annotation { "Feature Type Name" : "Feature", "Feature Type Description" : "" }
export const myFeature = defineFeature(function(context is Context, id is Id, definition is map)
    precondition{}
    {
        {
            var Q0;
            Q0=qCreatedBy(makeId("Front.planeOp"),FACE);
            var sketch = newSketch(context, id + "F0", { "sketchPlane" : qUnion([Q0])});
            skLineSegment(sketch, "E0", {"start": v(0, 0) * mm, "end": v(0, 220) * mm});
            skLineSegment(sketch, "E1", {"start": v(0, 220) * mm, "end": v(-210, 220) * mm});
            skLineSegment(sketch, "E2", {"start": v(-210, 220) * mm, "end": v(-210, 439.77) * mm});
            skLineSegment(sketch, "E3", {"start": v(-210, 439.77) * mm, "end": v(-420, 439.77) * mm});
            skLineSegment(sketch, "E4", {"start": v(-420, 660) * mm, "end": v(-630, 660) * mm});
            skLineSegment(sketch, "E5", {"start": v(-630, 660) * mm, "end": v(-630, 880) * mm});
            skLineSegment(sketch, "E6", {"start": v(-630, 880) * mm, "end": v(-840, 880) * mm});
            skLineSegment(sketch, "E7", {"start": v(-840, 880) * mm, "end": v(-840, 1100.35) * mm});
            skLineSegment(sketch, "E8", {"start": v(-840, 1100.35) * mm, "end": v(-1130, 1100.35) * mm});
            skLineSegment(sketch, "E9", {"start": v(-1130, 1100.35) * mm, "end": v(-1130, 1020.35) * mm});
            skLineSegment(sketch, "E10", {"start": v(-1130, 1020.35) * mm, "end": v(-920, 1020.35) * mm});
            skLineSegment(sketch, "E11", {"start": v(-920, 1020.35) * mm, "end": v(-920, 800.35) * mm});
            skLineSegment(sketch, "E12", {"start": v(-920, 800.35) * mm, "end": v(-710, 800.35) * mm});
            skLineSegment(sketch, "E13", {"start": v(-710, 800.35) * mm, "end": v(-710, 580.35) * mm});
            skLineSegment(sketch, "E14", {"start": v(-710, 580.35) * mm, "end": v(-500, 580.35) * mm});
            skLineSegment(sketch, "E15", {"start": v(-420, 660) * mm, "end": v(-420, 439.77) * mm});
            skLineSegment(sketch, "E16", {"start": v(-500, 580.35) * mm, "end": v(-500, 360.35) * mm});
            skLineSegment(sketch, "E17", {"start": v(-500, 360.35) * mm, "end": v(-290, 360.35) * mm});
            skLineSegment(sketch, "E18", {"start": v(-290, 360.35) * mm, "end": v(-290, 140.35) * mm});
            skLineSegment(sketch, "E19", {"start": v(-290, 140.35) * mm, "end": v(-80, 140.35) * mm});
            skLineSegment(sketch, "E20.top", {"start": v(-80, 0) * mm, "end": v(0, 0) * mm});
            skLineSegment(sketch, "E20.left", {"start": v(-80, 140.35) * mm, "end": v(-80, 0) * mm});
            skLineSegment(sketch, "E21.bottom", {"start": v(-2578.83, 300.57) * mm, "end": v(-2075.03, 300.57) * mm});
            skLineSegment(sketch, "E21.top", {"start": v(-2578.83, 380.57) * mm, "end": v(-2075.03, 380.57) * mm});
            skLineSegment(sketch, "E21.left", {"start": v(-2578.83, 300.57) * mm, "end": v(-2578.83, 380.57) * mm});
            skLineSegment(sketch, "E21.right", {"start": v(-2075.03, 300.57) * mm, "end": v(-2075.03, 380.57) * mm});
            skLineSegment(sketch, "E22.bottom", {"start": v(-2075.03, 300.57) * mm, "end": v(-2155.03, 300.57) * mm});
            skLineSegment(sketch, "E22.top", {"start": v(-2075.03, 160.57) * mm, "end": v(-2155.03, 160.57) * mm});
            skLineSegment(sketch, "E22.left", {"start": v(-2075.03, 300.57) * mm, "end": v(-2075.03, 160.57) * mm});
            skLineSegment(sketch, "E22.right", {"start": v(-2155.03, 300.57) * mm, "end": v(-2155.03, 160.57) * mm});
            skLineSegment(sketch, "E23.bottom", {"start": v(-1348.37, -189.05) * mm, "end": v(-782.17, -189.05) * mm});
            skLineSegment(sketch, "E23.top", {"start": v(-1348.37, -109.05) * mm, "end": v(-782.17, -109.05) * mm});
            skLineSegment(sketch, "E23.left", {"start": v(-1348.37, -189.05) * mm, "end": v(-1348.37, -109.05) * mm});
            skLineSegment(sketch, "E23.right", {"start": v(-782.17, -189.05) * mm, "end": v(-782.17, -109.05) * mm});
            skLineSegment(sketch, "E24.bottom", {"start": v(-782.17, -189.05) * mm, "end": v(-862.17, -189.05) * mm});
            skLineSegment(sketch, "E24.top", {"start": v(-782.17, -189.05) * mm, "end": v(-862.17, -189.05) * mm});
            skLineSegment(sketch, "E24.left", {"start": v(-782.17, -189.05) * mm, "end": v(-782.17, -189.05) * mm});
            skLineSegment(sketch, "E24.right", {"start": v(-862.17, -189.05) * mm, "end": v(-862.17, -189.05) * mm});
            skLineSegment(sketch, "E25.bottom", {"start": v(-210, -394.28) * mm, "end": v(-130, -394.28) * mm});
            skLineSegment(sketch, "E25.top", {"start": v(-210, -174.28) * mm, "end": v(-130, -174.28) * mm});
            skLineSegment(sketch, "E25.left", {"start": v(-210, -394.28) * mm, "end": v(-210, -174.28) * mm});
            skLineSegment(sketch, "E25.right", {"start": v(-130, -394.28) * mm, "end": v(-130, -174.28) * mm});
            skLineSegment(sketch, "E26.bottom", {"start": v(-130, -394.28) * mm, "end": v(-210, -394.28) * mm});
            skLineSegment(sketch, "E27.bottom", {"start": v(362.53, -433.02) * mm, "end": v(968.73, -433.02) * mm});
            skLineSegment(sketch, "E27.top", {"start": v(362.53, -353.02) * mm, "end": v(968.73, -353.02) * mm});
            skLineSegment(sketch, "E27.left", {"start": v(362.53, -433.02) * mm, "end": v(362.53, -353.02) * mm});
            skLineSegment(sketch, "E27.right", {"start": v(968.73, -433.02) * mm, "end": v(968.73, -353.02) * mm});
            skLineSegment(sketch, "E28.bottom", {"start": v(968.73, -433.02) * mm, "end": v(888.73, -433.02) * mm});
            skLineSegment(sketch, "E28.top", {"start": v(968.73, -573.02) * mm, "end": v(888.73, -573.02) * mm});
            skLineSegment(sketch, "E28.left", {"start": v(968.73, -433.02) * mm, "end": v(968.73, -573.02) * mm});
            skLineSegment(sketch, "E28.right", {"start": v(888.73, -433.02) * mm, "end": v(888.73, -573.02) * mm});
            skLineSegment(sketch, "E29.bottom", {"start": v(948.78, -109.9) * mm, "end": v(1442.58, -109.9) * mm});
            skLineSegment(sketch, "E29.top", {"start": v(948.78, -29.9) * mm, "end": v(1442.58, -29.9) * mm});
            skLineSegment(sketch, "E29.left", {"start": v(948.78, -109.9) * mm, "end": v(948.78, -29.9) * mm});
            skLineSegment(sketch, "E29.right", {"start": v(1442.58, -109.9) * mm, "end": v(1442.58, -29.9) * mm});
            skLineSegment(sketch, "E30.bottom", {"start": v(1442.58, -109.9) * mm, "end": v(1362.58, -109.9) * mm});
            skLineSegment(sketch, "E30.top", {"start": v(1442.58, -249.9) * mm, "end": v(1362.58, -249.9) * mm});
            skLineSegment(sketch, "E30.left", {"start": v(1442.58, -109.9) * mm, "end": v(1442.58, -249.9) * mm});
            skLineSegment(sketch, "E30.right", {"start": v(1362.58, -109.9) * mm, "end": v(1362.58, -249.9) * mm});
            skLineSegment(sketch, "E31.bottom", {"start": v(1819.6, 126.54) * mm, "end": v(2199.8, 126.54) * mm});
            skLineSegment(sketch, "E31.top", {"start": v(1819.6, 206.54) * mm, "end": v(2199.8, 206.54) * mm});
            skLineSegment(sketch, "E31.left", {"start": v(1819.6, 126.54) * mm, "end": v(1819.6, 206.54) * mm});
            skLineSegment(sketch, "E31.right", {"start": v(2199.8, 126.54) * mm, "end": v(2199.8, 206.54) * mm});
            skLineSegment(sketch, "E32.bottom", {"start": v(2199.8, 126.54) * mm, "end": v(2119.8, 126.54) * mm});
            skLineSegment(sketch, "E32.top", {"start": v(2199.8, -13.46) * mm, "end": v(2119.8, -13.46) * mm});
            skLineSegment(sketch, "E32.left", {"start": v(2199.8, 126.54) * mm, "end": v(2199.8, -13.46) * mm});
            skLineSegment(sketch, "E32.right", {"start": v(2119.8, 126.54) * mm, "end": v(2119.8, -13.46) * mm});
            skLineSegment(sketch, "E33.bottom", {"start": v(2564.96, -275.66) * mm, "end": v(2724.96, -275.66) * mm});
            skLineSegment(sketch, "E33.top", {"start": v(2564.96, -195.66) * mm, "end": v(2724.96, -195.66) * mm});
            skLineSegment(sketch, "E33.left", {"start": v(2564.96, -275.66) * mm, "end": v(2564.96, -195.66) * mm});
            skLineSegment(sketch, "E33.right", {"start": v(2724.96, -275.66) * mm, "end": v(2724.96, -195.66) * mm});
            skLineSegment(sketch, "E34.bottom", {"start": v(2724.96, -275.66) * mm, "end": v(2644.96, -275.66) * mm});
            skLineSegment(sketch, "E34.top", {"start": v(2724.96, -415.66) * mm, "end": v(2644.96, -415.66) * mm});
            skLineSegment(sketch, "E34.left", {"start": v(2724.96, -275.66) * mm, "end": v(2724.96, -415.66) * mm});
            skLineSegment(sketch, "E34.right", {"start": v(2644.96, -275.66) * mm, "end": v(2644.96, -415.66) * mm});
            skLineSegment(sketch, "E35.bottom", {"start": v(3270.46, -439.63) * mm, "end": v(3350.46, -439.63) * mm});
            skLineSegment(sketch, "E35.top", {"start": v(3270.46, -79.63) * mm, "end": v(3350.46, -79.63) * mm});
            skLineSegment(sketch, "E35.left", {"start": v(3270.46, -439.63) * mm, "end": v(3270.46, -79.63) * mm});
            skLineSegment(sketch, "E35.right", {"start": v(3350.46, -439.63) * mm, "end": v(3350.46, -79.63) * mm});
            skLineSegment(sketch, "E36.bottom", {"start": v(3922.36, -626.8) * mm, "end": v(4002.36, -626.8) * mm});
            skLineSegment(sketch, "E36.top", {"start": v(3922.36, -406.8) * mm, "end": v(4002.36, -406.8) * mm});
            skLineSegment(sketch, "E36.left", {"start": v(3922.36, -626.8) * mm, "end": v(3922.36, -406.8) * mm});
            skLineSegment(sketch, "E36.right", {"start": v(4002.36, -626.8) * mm, "end": v(4002.36, -406.8) * mm});
            skLineSegment(sketch, "E37.bottom", {"start": v(4584.73, -401.44) * mm, "end": v(4664.73, -401.44) * mm});
            skLineSegment(sketch, "E37.top", {"start": v(4584.73, -441.44) * mm, "end": v(4664.73, -441.44) * mm});
            skLineSegment(sketch, "E37.left", {"start": v(4584.73, -401.44) * mm, "end": v(4584.73, -441.44) * mm});
            skLineSegment(sketch, "E37.right", {"start": v(4664.73, -401.44) * mm, "end": v(4664.73, -441.44) * mm});
            skLineSegment(sketch, "E38.bottom", {"start": v(4664.73, -441.44) * mm, "end": v(4624.73, -441.44) * mm});
            skLineSegment(sketch, "E38.top", {"start": v(4664.73, -481.44) * mm, "end": v(4624.73, -481.44) * mm});
            skLineSegment(sketch, "E38.left", {"start": v(4664.73, -441.44) * mm, "end": v(4664.73, -481.44) * mm});
            skLineSegment(sketch, "E38.right", {"start": v(4624.73, -441.44) * mm, "end": v(4624.73, -481.44) * mm});
            skLineSegment(sketch, "E39.bottom", {"start": v(5084.64, -413.66) * mm, "end": v(5234.64, -413.66) * mm});
            skLineSegment(sketch, "E39.top", {"start": v(5084.64, -493.66) * mm, "end": v(5234.64, -493.66) * mm});
            skLineSegment(sketch, "E39.left", {"start": v(5084.64, -413.66) * mm, "end": v(5084.64, -493.66) * mm});
            skLineSegment(sketch, "E39.right", {"start": v(5234.64, -413.66) * mm, "end": v(5234.64, -493.66) * mm});
            skLineSegment(sketch, "E40.bottom", {"start": v(5234.64, -493.66) * mm, "end": v(5154.64, -493.66) * mm});
            skLineSegment(sketch, "E40.top", {"start": v(5234.64, -633.66) * mm, "end": v(5154.64, -633.66) * mm});
            skLineSegment(sketch, "E40.left", {"start": v(5234.64, -493.66) * mm, "end": v(5234.64, -633.66) * mm});
            skLineSegment(sketch, "E40.right", {"start": v(5154.64, -493.66) * mm, "end": v(5154.64, -633.66) * mm});
            skLineSegment(sketch, "E41.bottom", {"start": v(-1357.39, 3328.86) * mm, "end": v(-822.39, 3328.86) * mm});
            skLineSegment(sketch, "E41.top", {"start": v(-1357.39, 3408.86) * mm, "end": v(-822.39, 3408.86) * mm});
            skLineSegment(sketch, "E41.left", {"start": v(-1357.39, 3328.86) * mm, "end": v(-1357.39, 3408.86) * mm});
            skLineSegment(sketch, "E41.right", {"start": v(-822.39, 3328.86) * mm, "end": v(-822.39, 3408.86) * mm});
            skLineSegment(sketch, "E42.bottom", {"start": v(-822.39, 3328.86) * mm, "end": v(-902.39, 3328.86) * mm});
            skLineSegment(sketch, "E42.top", {"start": v(-822.39, 3188.86) * mm, "end": v(-902.39, 3188.86) * mm});
            skLineSegment(sketch, "E42.left", {"start": v(-822.39, 3328.86) * mm, "end": v(-822.39, 3188.86) * mm});
            skLineSegment(sketch, "E42.right", {"start": v(-902.39, 3328.86) * mm, "end": v(-902.39, 3188.86) * mm});
            skLineSegment(sketch, "E43.bottom", {"start": v(-362.9, 3377.98) * mm, "end": v(132.1, 3377.98) * mm});
            skLineSegment(sketch, "E43.top", {"start": v(-362.9, 3457.98) * mm, "end": v(132.1, 3457.98) * mm});
            skLineSegment(sketch, "E43.left", {"start": v(-362.9, 3377.98) * mm, "end": v(-362.9, 3457.98) * mm});
            skLineSegment(sketch, "E43.right", {"start": v(132.1, 3377.98) * mm, "end": v(132.1, 3457.98) * mm});
            skLineSegment(sketch, "E44.bottom", {"start": v(132.1, 3377.98) * mm, "end": v(52.1, 3377.98) * mm});
            skLineSegment(sketch, "E44.top", {"start": v(132.1, 3237.98) * mm, "end": v(52.1, 3237.98) * mm});
            skLineSegment(sketch, "E44.left", {"start": v(132.1, 3377.98) * mm, "end": v(132.1, 3237.98) * mm});
            skLineSegment(sketch, "E44.right", {"start": v(52.1, 3377.98) * mm, "end": v(52.1, 3237.98) * mm});
            skLineSegment(sketch, "E45.bottom", {"start": v(416.79, 3352.05) * mm, "end": v(931.79, 3352.05) * mm});
            skLineSegment(sketch, "E45.top", {"start": v(416.79, 3432.05) * mm, "end": v(931.79, 3432.05) * mm});
            skLineSegment(sketch, "E45.left", {"start": v(416.79, 3352.05) * mm, "end": v(416.79, 3432.05) * mm});
            skLineSegment(sketch, "E45.right", {"start": v(931.79, 3352.05) * mm, "end": v(931.79, 3432.05) * mm});
            skLineSegment(sketch, "E46.bottom", {"start": v(931.79, 3352.05) * mm, "end": v(851.79, 3352.05) * mm});
            skLineSegment(sketch, "E46.top", {"start": v(931.79, 3132.05) * mm, "end": v(851.79, 3132.05) * mm});
            skLineSegment(sketch, "E46.left", {"start": v(931.79, 3352.05) * mm, "end": v(931.79, 3132.05) * mm});
            skLineSegment(sketch, "E46.right", {"start": v(851.79, 3352.05) * mm, "end": v(851.79, 3132.05) * mm});
            skLineSegment(sketch, "E47.bottom", {"start": v(1406.19, 3471.6) * mm, "end": v(1841.19, 3471.6) * mm});
            skLineSegment(sketch, "E47.top", {"start": v(1406.19, 3551.6) * mm, "end": v(1841.19, 3551.6) * mm});
            skLineSegment(sketch, "E47.left", {"start": v(1406.19, 3471.6) * mm, "end": v(1406.19, 3551.6) * mm});
            skLineSegment(sketch, "E47.right", {"start": v(1841.19, 3471.6) * mm, "end": v(1841.19, 3551.6) * mm});
            skLineSegment(sketch, "E48.bottom", {"start": v(1841.19, 3471.6) * mm, "end": v(1761.19, 3471.6) * mm});
            skLineSegment(sketch, "E48.top", {"start": v(1841.19, 3331.6) * mm, "end": v(1761.19, 3331.6) * mm});
            skLineSegment(sketch, "E48.left", {"start": v(1841.19, 3471.6) * mm, "end": v(1841.19, 3331.6) * mm});
            skLineSegment(sketch, "E48.right", {"start": v(1761.19, 3471.6) * mm, "end": v(1761.19, 3331.6) * mm});
            skLineSegment(sketch, "E49.bottom", {"start": v(2616.38, 4182.89) * mm, "end": v(2536.38, 4182.89) * mm});
            skLineSegment(sketch, "E49.top", {"start": v(2616.38, 3302.89) * mm, "end": v(2536.38, 3302.89) * mm});
            skLineSegment(sketch, "E49.left", {"start": v(2616.38, 4182.89) * mm, "end": v(2616.38, 3302.89) * mm});
            skLineSegment(sketch, "E49.right", {"start": v(2536.38, 4182.89) * mm, "end": v(2536.38, 3302.89) * mm});
            skSolve(sketch);
        }
        {
            var Q0;
            Q0=qSketchRegion(id+"F0",true);
            extrude(context, id + "F1", {"entities" : qUnion([Q0]), "depth" : 40 * mm, "offsetDistance" : 25 * mm});
        }
        {
            var Q0;
            Q0=qCreatedBy(makeId("Front.planeOp"),FACE);
            var sketch = newSketch(context, id + "F2", { "sketchPlane" : qUnion([Q0])});
            skLineSegment(sketch, "E50.bottom", {"start": v(-682.97, -92.7) * mm, "end": v(-432.97, -92.7) * mm});
            skLineSegment(sketch, "E50.top", {"start": v(-682.97, -132.7) * mm, "end": v(-432.97, -132.7) * mm});
            skLineSegment(sketch, "E50.left", {"start": v(-682.97, -92.7) * mm, "end": v(-682.97, -132.7) * mm});
            skLineSegment(sketch, "E50.right", {"start": v(-432.97, -92.7) * mm, "end": v(-432.97, -132.7) * mm});
            skSolve(sketch);
        }
        {
            var Q0;
            Q0=makeQuery(id+"F2.imprint","IMPRINT",FACE,{"disambiguationData":[TD([[makeQuery(id+"F2.imprint","IMPRINT",EDGE,{"derivedFrom":sQuery(id+"F2.wireOp",EDGE,"E50.bottom")}),-1.0]])]});
            extrude(context, id + "F3", {"entities" : qUnion([Q0]), "depth" : 830 * mm, "offsetDistance" : 25 * mm});
        }
        {
            var Q0;
            Q0=qCreatedBy(makeId("Top.planeOp"),FACE);
            var sketch = newSketch(context, id + "F4", { "sketchPlane" : qUnion([Q0])});
            skLineSegment(sketch, "E51.top", {"start": v(-47.98, 505.23) * mm, "end": v(812.02, 505.23) * mm});
            skLineSegment(sketch, "E51.right", {"start": v(812.02, -544.77) * mm, "end": v(812.02, 505.23) * mm});
            skLineSegment(sketch, "E52", {"start": v(-47.98, -374.77) * mm, "end": v(-47.98, 505.23) * mm});
            skLineSegment(sketch, "E53", {"start": v(32.02, -544.77) * mm, "end": v(812.02, -544.77) * mm});
            skLineSegment(sketch, "E54", {"start": v(32.02, -518.77) * mm, "end": v(812.02, -265.33) * mm});
            skLineSegment(sketch, "E55", {"start": v(32.02, -486.64) * mm, "end": v(812.02, 80.06) * mm});
            skLineSegment(sketch, "E56", {"start": v(32.02, -434.66) * mm, "end": v(714.89, 505.23) * mm});
            skLineSegment(sketch, "E57", {"start": v(7.26, -374.77) * mm, "end": v(293.18, 505.23) * mm});
            skLineSegment(sketch, "E58.top", {"start": v(-47.98, -374.77) * mm, "end": v(32.02, -374.77) * mm});
            skLineSegment(sketch, "E58.right", {"start": v(32.02, -544.77) * mm, "end": v(32.02, -374.77) * mm});
            skLineSegment(sketch, "E59.top", {"start": v(-2332.02, 1857.89) * mm, "end": v(-1472.02, 1857.89) * mm});
            skLineSegment(sketch, "E59.right", {"start": v(-1472.02, 807.89) * mm, "end": v(-1472.02, 1857.89) * mm});
            skLineSegment(sketch, "E60", {"start": v(-2332.02, 807.89) * mm, "end": v(-2332.02, 1857.89) * mm});
            skLineSegment(sketch, "E61", {"start": v(-2332.02, 807.89) * mm, "end": v(-1472.02, 807.89) * mm});
            skLineSegment(sketch, "E62", {"start": v(-2332.02, 807.89) * mm, "end": v(-618.07, 1364.79) * mm});
            skLineSegment(sketch, "E63", {"start": v(-2332.02, 807.89) * mm, "end": v(-904.42, 1845.1) * mm});
            skLineSegment(sketch, "E64", {"start": v(-2332.02, 807.89) * mm, "end": v(-1124.73, 2469.58) * mm});
            skLineSegment(sketch, "E65", {"start": v(-2332.02, 807.89) * mm, "end": v(-1660.21, 2875.5) * mm});
            skLineSegment(sketch, "E66.bottom", {"start": v(-2332.02, 807.89) * mm, "end": v(-1818.46, 807.89) * mm});
            skLineSegment(sketch, "E66.top", {"start": v(-2332.02, 1051.9) * mm, "end": v(-1818.46, 1051.9) * mm});
            skLineSegment(sketch, "E66.left", {"start": v(-2332.02, 807.89) * mm, "end": v(-2332.02, 1051.9) * mm});
            skLineSegment(sketch, "E66.right", {"start": v(-1818.46, 807.89) * mm, "end": v(-1818.46, 1051.9) * mm});
            skLineSegment(sketch, "E67.top", {"start": v(1615.02, -757.08) * mm, "end": v(2475.02, -757.08) * mm});
            skLineSegment(sketch, "E67.right", {"start": v(2475.02, -1807.08) * mm, "end": v(2475.02, -757.08) * mm});
            skLineSegment(sketch, "E68", {"start": v(1615.02, -1807.08) * mm, "end": v(1615.02, -757.08) * mm});
            skLineSegment(sketch, "E69", {"start": v(1615.02, -1807.08) * mm, "end": v(2475.02, -1807.08) * mm});
            skLineSegment(sketch, "E70", {"start": v(1615.02, -1807.08) * mm, "end": v(3328.97, -1250.18) * mm});
            skLineSegment(sketch, "E71", {"start": v(1615.02, -1807.08) * mm, "end": v(3042.62, -769.87) * mm});
            skLineSegment(sketch, "E72", {"start": v(1615.02, -1807.08) * mm, "end": v(2822.3, -145.4) * mm});
            skLineSegment(sketch, "E73", {"start": v(1615.02, -1807.08) * mm, "end": v(2286.82, 260.52) * mm});
            skLineSegment(sketch, "E74.bottom", {"start": v(1615.02, -1807.08) * mm, "end": v(1695.02, -1807.08) * mm});
            skLineSegment(sketch, "E74.top", {"start": v(1615.02, -1637.08) * mm, "end": v(1695.02, -1637.08) * mm});
            skLineSegment(sketch, "E74.left", {"start": v(1615.02, -1807.08) * mm, "end": v(1615.02, -1637.08) * mm});
            skLineSegment(sketch, "E74.right", {"start": v(1695.02, -1807.08) * mm, "end": v(1695.02, -1637.08) * mm});
            skLineSegment(sketch, "E75.right", {"start": v(472.23, -2101.59) * mm, "end": v(472.23, -1822.16) * mm});
            skLineSegment(sketch, "E76", {"start": v(-307.77, -2101.59) * mm, "end": v(472.23, -2101.59) * mm});
            skLineSegment(sketch, "E77", {"start": v(-307.77, -2075.6) * mm, "end": v(472.23, -1822.16) * mm});
            skLineSegment(sketch, "E78", {"start": v(-307.77, -2043.46) * mm, "end": v(472.23, -1476.76) * mm});
            skLineSegment(sketch, "E79", {"start": v(-332.53, -1931.59) * mm, "end": v(-46.6, -1051.59) * mm});
            skLineSegment(sketch, "E80.right", {"start": v(-307.77, -2101.59) * mm, "end": v(-307.77, -2075.6) * mm});
            skLineSegment(sketch, "E81.trimOffspring", {"start": v(472.23, -1476.76) * mm, "end": v(472.23, -1051.59) * mm});
            skLineSegment(sketch, "E82", {"start": v(-653.82, -4085.18) * mm, "end": v(29.05, -3145.3) * mm});
            skLineSegment(sketch, "E83.trimOffspring", {"start": v(-653.82, -4085.18) * mm, "end": v(-653.82, -4025.3) * mm});
            skLineSegment(sketch, "E84.0", {"start": v(-462.27, -1931.59) * mm, "end": v(-462.27, -1051.59) * mm});
            skLineSegment(sketch, "E85", {"start": v(-462.27, -1931.59) * mm, "end": v(-332.53, -1931.59) * mm});
            skLineSegment(sketch, "E86", {"start": v(-462.27, -1051.59) * mm, "end": v(-46.6, -1051.59) * mm});
            skText(sketch, "E87", { "text": "GOTOWE\n", "fontName": "OpenSans-Regular.ttf"});
            skLineSegment(sketch, "E88", {"start": v(-653.82, -4025.3) * mm, "end": v(-720.64, -4025.3) * mm});
            skLineSegment(sketch, "E89", {"start": v(-434.71, -3145.3) * mm, "end": v(29.05, -3145.3) * mm});
            skLineSegment(sketch, "E90", {"start": v(-720.64, -4025.3) * mm, "end": v(-434.71, -3145.3) * mm});
            skLineSegment(sketch, "E91.0", {"start": v(-307.77, -1923.42) * mm, "end": v(325.66, -1051.59) * mm});
            skLineSegment(sketch, "E92", {"start": v(325.66, -1051.59) * mm, "end": v(472.23, -1051.59) * mm});
            skLineSegment(sketch, "E93", {"start": v(-307.77, -1923.42) * mm, "end": v(-307.77, -2043.46) * mm});
            skLineSegment(sketch, "E94.right", {"start": v(1369.34, -4712.42) * mm, "end": v(1369.34, -4367.03) * mm});
            skLineSegment(sketch, "E95", {"start": v(589.34, -4965.86) * mm, "end": v(1369.34, -4712.42) * mm});
            skLineSegment(sketch, "E96.right", {"start": v(589.34, -4965.86) * mm, "end": v(589.34, -4933.73) * mm});
            skLineSegment(sketch, "E97", {"start": v(589.34, -4933.73) * mm, "end": v(589.34, -4884.29) * mm});
            skLineSegment(sketch, "E98", {"start": v(1369.34, -4367.03) * mm, "end": v(1369.34, -4317.58) * mm});
            skLineSegment(sketch, "E99", {"start": v(589.34, -4884.29) * mm, "end": v(1369.34, -4317.58) * mm});
            skLineSegment(sketch, "E100.right", {"start": v(-1409.89, -2528.05) * mm, "end": v(-1409.89, -2248.62) * mm});
            skLineSegment(sketch, "E101", {"start": v(-2189.89, -2528.05) * mm, "end": v(-1409.89, -2528.05) * mm});
            skLineSegment(sketch, "E102.right", {"start": v(-2189.89, -2528.05) * mm, "end": v(-2189.89, -2502.06) * mm});
            skLineSegment(sketch, "E103.0", {"start": v(-2189.89, -2460) * mm, "end": v(-1422.25, -2210.58) * mm});
            skLineSegment(sketch, "E104", {"start": v(-2189.89, -2528.05) * mm, "end": v(-2189.89, -2460) * mm});
            skLineSegment(sketch, "E105", {"start": v(-1409.89, -2528.05) * mm, "end": v(-1409.89, -2206.56) * mm});
            skLineSegment(sketch, "E106", {"start": v(-1422.25, -2210.58) * mm, "end": v(-1409.89, -2206.56) * mm});
            skLineSegment(sketch, "E107.top", {"start": v(4345.64, 540.9) * mm, "end": v(4775.64, 540.9) * mm});
            skLineSegment(sketch, "E107.left", {"start": v(4345.64, 80.9) * mm, "end": v(4345.64, 540.9) * mm});
            skLineSegment(sketch, "E107.right", {"start": v(5205.64, -379.1) * mm, "end": v(5205.64, 540.9) * mm});
            skLineSegment(sketch, "E108", {"start": v(5205.64, -379.1) * mm, "end": v(4345.64, -379.1) * mm});
            skLineSegment(sketch, "E109", {"start": v(5205.64, -379.1) * mm, "end": v(4345.64, 540.9) * mm});
            skLineSegment(sketch, "E110", {"start": v(5205.64, -379.1) * mm, "end": v(4345.64, 80.9) * mm});
            skLineSegment(sketch, "E111", {"start": v(5205.64, -379.1) * mm, "end": v(4775.64, 540.9) * mm});
            skLineSegment(sketch, "E112", {"start": v(4775.64, 540.9) * mm, "end": v(5205.64, 540.9) * mm});
            skPoint(sketch, "E113.orphan", {"position": v(4345.64, -379.1) * mm});
            skLineSegment(sketch, "E114", {"start": v(4345.64, 80.9) * mm, "end": v(4345.64, -379.1) * mm});
            skLineSegment(sketch, "E115.bottom", {"start": v(5205.64, -379.1) * mm, "end": v(5125.64, -379.1) * mm});
            skLineSegment(sketch, "E115.top", {"start": v(5205.64, -339.1) * mm, "end": v(5125.64, -339.1) * mm});
            skLineSegment(sketch, "E115.left", {"start": v(5205.64, -379.1) * mm, "end": v(5205.64, -339.1) * mm});
            skLineSegment(sketch, "E115.right", {"start": v(5125.64, -379.1) * mm, "end": v(5125.64, -339.1) * mm});
            skLineSegment(sketch, "E116.right", {"start": v(9124.54, 1333.6) * mm, "end": v(9124.54, 2213.6) * mm});
            skLineSegment(sketch, "E117", {"start": v(8694.54, 2213.6) * mm, "end": v(9124.54, 2213.6) * mm});
            skLineSegment(sketch, "E118.top", {"start": v(9124.54, 1333.6) * mm, "end": v(9105.84, 1333.6) * mm});
            skLineSegment(sketch, "E119", {"start": v(10139.01, 171.77) * mm, "end": v(9316.4, 1051.77) * mm});
            skLineSegment(sketch, "E120.top", {"start": v(9713.88, 2351.53) * mm, "end": v(10143.88, 2351.53) * mm});
            skLineSegment(sketch, "E121", {"start": v(10555.18, 1471.53) * mm, "end": v(10143.88, 2351.53) * mm});
            skLineSegment(sketch, "E122.top", {"start": v(10555.18, 1471.53) * mm, "end": v(10536.49, 1471.53) * mm});
            skLineSegment(sketch, "E123", {"start": v(12382.63, 807.89) * mm, "end": v(11602.63, 807.89) * mm});
            skLineSegment(sketch, "E124", {"start": v(12387.85, 847.89) * mm, "end": v(11602.63, 1267.89) * mm});
            skPoint(sketch, "E125.orphan", {"position": v(11602.63, 807.89) * mm});
            skLineSegment(sketch, "E126", {"start": v(11602.63, 1267.89) * mm, "end": v(11602.63, 807.89) * mm});
            skLineSegment(sketch, "E127.right", {"start": v(12382.63, 807.89) * mm, "end": v(12382.63, 847.89) * mm});
            skLineSegment(sketch, "E128.trimOffspring", {"start": v(10139.01, 171.77) * mm, "end": v(10101.62, 171.77) * mm});
            skLineSegment(sketch, "E129.trimOffspring", {"start": v(12387.85, 847.89) * mm, "end": v(12382.63, 847.89) * mm});
            skLineSegment(sketch, "E130.0", {"start": v(9061.69, 1333.6) * mm, "end": v(8658.77, 2195.65) * mm});
            skLineSegment(sketch, "E131", {"start": v(8694.54, 2213.6) * mm, "end": v(8650.38, 2213.6) * mm});
            skLineSegment(sketch, "E132", {"start": v(9105.84, 1333.6) * mm, "end": v(9061.69, 1333.6) * mm});
            skLineSegment(sketch, "E133", {"start": v(8658.77, 2195.65) * mm, "end": v(8650.38, 2213.6) * mm});
            skLineSegment(sketch, "E134.0", {"start": v(10481.73, 1471.53) * mm, "end": v(9713.88, 2292.96) * mm});
            skLineSegment(sketch, "E135", {"start": v(10536.49, 1471.53) * mm, "end": v(10481.73, 1471.53) * mm});
            skLineSegment(sketch, "E136.0", {"start": v(10016.81, 171.77) * mm, "end": v(9316.4, 546.4) * mm});
            skLineSegment(sketch, "E137", {"start": v(10101.62, 171.77) * mm, "end": v(10016.81, 171.77) * mm});
            skLineSegment(sketch, "E138", {"start": v(9316.4, 1051.77) * mm, "end": v(9316.4, 546.4) * mm});
            skLineSegment(sketch, "E139", {"start": v(9713.88, 2351.53) * mm, "end": v(9713.88, 2292.96) * mm});
            skLineSegment(sketch, "E140", {"start": v(3639.4, -6062.46) * mm, "end": v(4419.4, -5495.76) * mm});
            skLineSegment(sketch, "E141.trimOffspring", {"start": v(4419.4, -5495.76) * mm, "end": v(4419.4, -5070.59) * mm});
            skLineSegment(sketch, "E142.0", {"start": v(3639.4, -5942.42) * mm, "end": v(4272.84, -5070.59) * mm});
            skLineSegment(sketch, "E143", {"start": v(4272.84, -5070.59) * mm, "end": v(4419.4, -5070.59) * mm});
            skLineSegment(sketch, "E144", {"start": v(3639.4, -5942.42) * mm, "end": v(3639.4, -6062.46) * mm});
            skLineSegment(sketch, "E145", {"start": v(7082.91, -6742.24) * mm, "end": v(7368.84, -5862.24) * mm});
            skLineSegment(sketch, "E146.0", {"start": v(6953.17, -6742.24) * mm, "end": v(6953.17, -5862.24) * mm});
            skLineSegment(sketch, "E147", {"start": v(6953.17, -6742.24) * mm, "end": v(7082.91, -6742.24) * mm});
            skLineSegment(sketch, "E148", {"start": v(6953.17, -5862.24) * mm, "end": v(7368.84, -5862.24) * mm});
            skLineSegment(sketch, "E149.bottom", {"start": v(3060.13, 3977.35) * mm, "end": v(3970.13, 3977.35) * mm});
            skLineSegment(sketch, "E149.top", {"start": v(3060.13, 4847.35) * mm, "end": v(3970.13, 4847.35) * mm});
            skLineSegment(sketch, "E149.left", {"start": v(3060.13, 3977.35) * mm, "end": v(3060.13, 4847.35) * mm});
            skLineSegment(sketch, "E149.right", {"start": v(3970.13, 3977.35) * mm, "end": v(3970.13, 4847.35) * mm});
            skLineSegment(sketch, "E150", {"start": v(3060.13, 4847.35) * mm, "end": v(3060.13, 5144) * mm});
            skLineSegment(sketch, "E151.0", {"start": v(3515.13, 4847.35) * mm, "end": v(3515.13, 5144) * mm});
            skLineSegment(sketch, "E152", {"start": v(3060.13, 4847.35) * mm, "end": v(2788.73, 4847.35) * mm});
            skLineSegment(sketch, "E153.0", {"start": v(3060.13, 4412.35) * mm, "end": v(2788.73, 4412.35) * mm});
            skLineSegment(sketch, "E154", {"start": v(3970.13, 3977.35) * mm, "end": v(3515.13, 4847.35) * mm});
            skLineSegment(sketch, "E155", {"start": v(3970.13, 3977.35) * mm, "end": v(3060.13, 4847.35) * mm});
            skLineSegment(sketch, "E156", {"start": v(3970.13, 3977.35) * mm, "end": v(3060.13, 4412.35) * mm});
            skLineSegment(sketch, "E157.top", {"start": v(5206.12, 5104.66) * mm, "end": v(5661.12, 5104.66) * mm});
            skLineSegment(sketch, "E157.right", {"start": v(5661.12, 4274.66) * mm, "end": v(5661.12, 5104.66) * mm});
            skLineSegment(sketch, "E158.top", {"start": v(5661.12, 4274.66) * mm, "end": v(5595.06, 4274.66) * mm});
            skLineSegment(sketch, "E159.bottom", {"start": v(3970.13, 3977.35) * mm, "end": v(3890.13, 3977.35) * mm});
            skLineSegment(sketch, "E159.top", {"start": v(3970.13, 4017.35) * mm, "end": v(3890.13, 4017.35) * mm});
            skLineSegment(sketch, "E159.left", {"start": v(3970.13, 3977.35) * mm, "end": v(3970.13, 4017.35) * mm});
            skLineSegment(sketch, "E159.right", {"start": v(3890.13, 3977.35) * mm, "end": v(3890.13, 4017.35) * mm});
            skLineSegment(sketch, "E160", {"start": v(5206.12, 5104.66) * mm, "end": v(5160.98, 5104.66) * mm});
            skLineSegment(sketch, "E161", {"start": v(5170.68, 5086.12) * mm, "end": v(5189.55, 5050.03) * mm});
            skLineSegment(sketch, "E162", {"start": v(5189.55, 5050.03) * mm, "end": v(5160.98, 5104.66) * mm});
            skLineSegment(sketch, "E163.trimOffspring", {"start": v(5595.06, 4274.66) * mm, "end": v(5170.68, 5086.12) * mm});
            skLineSegment(sketch, "E164.top", {"start": v(6822.3, 5560.33) * mm, "end": v(7277.3, 5560.33) * mm});
            skLineSegment(sketch, "E164.left", {"start": v(6822.3, 5505) * mm, "end": v(6822.3, 5560.33) * mm});
            skLineSegment(sketch, "E165", {"start": v(7711.38, 4730.33) * mm, "end": v(7277.3, 5560.33) * mm});
            skLineSegment(sketch, "E166.top", {"start": v(7711.38, 4730.33) * mm, "end": v(7652.3, 4730.33) * mm});
            skLineSegment(sketch, "E166.right", {"start": v(7652.3, 4711.48) * mm, "end": v(7652.3, 4730.33) * mm});
            skLineSegment(sketch, "E167.trimOffspring", {"start": v(7652.3, 4711.48) * mm, "end": v(6822.3, 5505) * mm});
            skLineSegment(sketch, "E168.left", {"start": v(8733.66, 5429.45) * mm, "end": v(8733.66, 5908.78) * mm});
            skLineSegment(sketch, "E169", {"start": v(9601.82, 5078.78) * mm, "end": v(8733.66, 5908.78) * mm});
            skLineSegment(sketch, "E170.right", {"start": v(9563.66, 5038.78) * mm, "end": v(9563.66, 5078.78) * mm});
            skLineSegment(sketch, "E171.trimOffspring", {"start": v(9601.82, 5078.78) * mm, "end": v(9563.66, 5078.78) * mm});
            skLineSegment(sketch, "E172.0", {"start": v(9546.41, 5040.93) * mm, "end": v(8733.66, 5429.45) * mm});
            skLineSegment(sketch, "E173", {"start": v(9563.66, 5038.78) * mm, "end": v(9550.91, 5038.78) * mm});
            skLineSegment(sketch, "E174", {"start": v(9546.41, 5040.93) * mm, "end": v(9550.91, 5038.78) * mm});
            skLineSegment(sketch, "E175.bottom", {"start": v(10726.24, 5385.35) * mm, "end": v(11556.24, 5385.35) * mm});
            skLineSegment(sketch, "E175.left", {"start": v(10726.24, 5385.35) * mm, "end": v(10726.24, 5820.35) * mm});
            skLineSegment(sketch, "E176", {"start": v(11556.24, 5423.6) * mm, "end": v(10726.24, 5820.35) * mm});
            skLineSegment(sketch, "E177.right", {"start": v(11556.24, 5385.35) * mm, "end": v(11556.24, 5423.6) * mm});
            const initialGuessF4  = {"E87": [4.11145, -3.47683, 1, 0, 0.4424]};
            skSetInitialGuess(sketch, initialGuessF4);
            skSolve(sketch);
        }
        {
            var Q0;
            Q0=makeQuery(id+"F4.imprint","IMPRINT",FACE,{"disambiguationData":[TD([[makeQuery(id+"F4.imprint","IMPRINT",EDGE,{"derivedFrom":sQuery(id+"F4.wireOp",EDGE,"E79")}),1.0]])]});
            extrude(context, id + "F5", {"entities" : qUnion([Q0]), "depth" : 40 * mm, "offsetDistance" : 25 * mm});
        }
        {
            var Q0;
            Q0=makeQuery(id+"F4.imprint","IMPRINT",FACE,{"disambiguationData":[TD([[makeQuery(id+"F4.imprint","IMPRINT",EDGE,{"derivedFrom":sQuery(id+"F4.wireOp",EDGE,"E82")}),1.0]])]});
            extrude(context, id + "F6", {"entities" : qUnion([Q0]), "depth" : 40 * mm, "offsetDistance" : 25 * mm});
        }
        {
            var Q0;
            Q0=makeQuery(id+"F4.imprint","IMPRINT",FACE,{"disambiguationData":[TD([[makeQuery(id+"F4.imprint","IMPRINT",EDGE,{"derivedFrom":sQuery(id+"F4.wireOp",EDGE,"E78")}),1.0]])]});
            extrude(context, id + "F7", {"entities" : qUnion([Q0]), "depth" : 40 * mm, "offsetDistance" : 25 * mm});
        }
        {
            var Q0;
            Q0=makeQuery(id+"F4.imprint","IMPRINT",FACE,{"disambiguationData":[TD([[makeQuery(id+"F4.imprint","IMPRINT",EDGE,{"derivedFrom":sQuery(id+"F4.wireOp",EDGE,"E94.right")}),1.0]])]});
            extrude(context, id + "F8", {"entities" : qUnion([Q0]), "depth" : 40 * mm, "offsetDistance" : 25 * mm});
        }
        {
            var Q0;
            {var subQ3=sQuery(id+"F4.wireOp",EDGE,"E101");Q0=makeQuery(id+"F4.imprint","IMPRINT",FACE,{"disambiguationData":[TD([[makeQuery(id+"F4.imprint","IMPRINT",EDGE,{"derivedFrom":subQ3}),1.0]])]});}
            extrude(context, id + "F9", {"entities" : qUnion([Q0]), "depth" : 40 * mm, "offsetDistance" : 25 * mm});
        }
        {
            var Q0;
            Q0=makeQuery(id+"F4.imprint","IMPRINT",FACE,{"disambiguationData":[TD([[makeQuery(id+"F4.imprint","IMPRINT",EDGE,{"derivedFrom":sQuery(id+"F4.wireOp",EDGE,"E116.right")}),1.0]])]});
            extrude(context, id + "F10", {"entities" : qUnion([Q0]), "depth" : 40 * mm, "offsetDistance" : 25 * mm});
        }
        {
            var Q0;
            Q0=makeQuery(id+"F4.imprint","IMPRINT",FACE,{"disambiguationData":[TD([[makeQuery(id+"F4.imprint","IMPRINT",EDGE,{"derivedFrom":sQuery(id+"F4.wireOp",EDGE,"E120.top")}),-1.0]])]});
            extrude(context, id + "F11", {"entities" : qUnion([Q0]), "depth" : 25 * mm, "offsetDistance" : 25 * mm});
        }
        {
            var Q0;
            Q0=makeQuery(id+"F4.imprint","IMPRINT",FACE,{"disambiguationData":[TD([[makeQuery(id+"F4.imprint","IMPRINT",EDGE,{"derivedFrom":sQuery(id+"F4.wireOp",EDGE,"E119")}),1.0]])]});
            extrude(context, id + "F12", {"entities" : qUnion([Q0]), "depth" : 40 * mm, "offsetDistance" : 25 * mm});
        }
        {
            var Q0;
            Q0=makeQuery(id+"F4.imprint","IMPRINT",FACE,{"disambiguationData":[TD([[makeQuery(id+"F4.imprint","IMPRINT",EDGE,{"derivedFrom":sQuery(id+"F4.wireOp",EDGE,"E123")}),-1.0]])]});
            extrude(context, id + "F13", {"entities" : qUnion([Q0]), "depth" : 40 * mm, "offsetDistance" : 25 * mm});
        }
        {
            var Q0;
            Q0=makeQuery(id+"F0.imprint","IMPRINT",FACE,{"disambiguationData":[TD([[makeQuery(id+"F0.imprint","IMPRINT",EDGE,{"derivedFrom":sQuery(id+"F0.wireOp",EDGE,"E22.bottom")}),1.0]])]});
            var Q1;
            Q1=makeQuery(id+"F0.imprint","IMPRINT",FACE,{"disambiguationData":[TD([[makeQuery(id+"F0.imprint","IMPRINT",EDGE,{"derivedFrom":sQuery(id+"F0.wireOp",EDGE,"E21.bottom")}),1.0]])]});
            extrude(context, id + "F14", {"entities" : qUnion([Q0, Q1]), "operationType" : NewBodyOperationType.ADD, "depth" : 40 * mm, "offsetDistance" : 25 * mm});
        }
        {
            var Q0;
            Q0=makeQuery(id+"F0.imprint","IMPRINT",FACE,{"disambiguationData":[TD([[makeQuery(id+"F0.imprint","IMPRINT",EDGE,{"derivedFrom":sQuery(id+"F0.wireOp",EDGE,"E23.bottom")}),1.0]])]});
            var Q1;
            Q1=makeQuery(id+"F0.imprint","IMPRINT",FACE,{"disambiguationData":[TD([[makeQuery(id+"F0.imprint","IMPRINT",EDGE,{"derivedFrom":sQuery(id+"F0.wireOp",EDGE,"E24.bottom")}),1.0]])]});
            extrude(context, id + "F15", {"entities" : qUnion([Q0, Q1]), "operationType" : NewBodyOperationType.ADD, "depth" : 40 * mm, "offsetDistance" : 25 * mm});
        }
        {
            var Q0;
            Q0=makeQuery(id+"F0.imprint","IMPRINT",FACE,{"disambiguationData":[TD([[makeQuery(id+"F0.imprint","IMPRINT",EDGE,{"derivedFrom":sQuery(id+"F0.wireOp",EDGE,"E25.bottom")}),1.0]])]});
            var Q1;
            Q1=makeQuery(id+"F0.imprint","IMPRINT",FACE,{"disambiguationData":[TD([[makeQuery(id+"F0.imprint","IMPRINT",EDGE,{"derivedFrom":sQuery(id+"F0.wireOp",EDGE,"E26.bottom")}),1.0]])]});
            extrude(context, id + "F16", {"entities" : qUnion([Q0, Q1]), "operationType" : NewBodyOperationType.ADD, "depth" : 40 * mm, "offsetDistance" : 25 * mm});
        }
        {
            var Q0;
            Q0=makeQuery(id+"F0.imprint","IMPRINT",FACE,{"disambiguationData":[TD([[makeQuery(id+"F0.imprint","IMPRINT",EDGE,{"derivedFrom":sQuery(id+"F0.wireOp",EDGE,"E27.bottom")}),1.0]])]});
            var Q1;
            Q1=makeQuery(id+"F0.imprint","IMPRINT",FACE,{"disambiguationData":[TD([[makeQuery(id+"F0.imprint","IMPRINT",EDGE,{"derivedFrom":sQuery(id+"F0.wireOp",EDGE,"E28.bottom")}),1.0]])]});
            extrude(context, id + "F17", {"entities" : qUnion([Q0, Q1]), "operationType" : NewBodyOperationType.ADD, "depth" : 40 * mm, "offsetDistance" : 25 * mm});
        }
        {
            var Q0;
            Q0=makeQuery(id+"F0.imprint","IMPRINT",FACE,{"disambiguationData":[TD([[makeQuery(id+"F0.imprint","IMPRINT",EDGE,{"derivedFrom":sQuery(id+"F0.wireOp",EDGE,"E29.bottom")}),1.0]])]});
            var Q1;
            Q1=makeQuery(id+"F0.imprint","IMPRINT",FACE,{"disambiguationData":[TD([[makeQuery(id+"F0.imprint","IMPRINT",EDGE,{"derivedFrom":sQuery(id+"F0.wireOp",EDGE,"E30.bottom")}),1.0]])]});
            extrude(context, id + "F18", {"entities" : qUnion([Q0, Q1]), "operationType" : NewBodyOperationType.ADD, "depth" : 40 * mm, "offsetDistance" : 25 * mm});
        }
        {
            var Q0;
            Q0=makeQuery(id+"F0.imprint","IMPRINT",FACE,{"disambiguationData":[TD([[makeQuery(id+"F0.imprint","IMPRINT",EDGE,{"derivedFrom":sQuery(id+"F0.wireOp",EDGE,"E31.bottom")}),1.0]])]});
            var Q1;
            Q1=makeQuery(id+"F0.imprint","IMPRINT",FACE,{"disambiguationData":[TD([[makeQuery(id+"F0.imprint","IMPRINT",EDGE,{"derivedFrom":sQuery(id+"F0.wireOp",EDGE,"E32.bottom")}),1.0]])]});
            extrude(context, id + "F19", {"entities" : qUnion([Q0, Q1]), "operationType" : NewBodyOperationType.ADD, "depth" : 40 * mm, "offsetDistance" : 25 * mm});
        }
        {
            var Q0;
            Q0=makeQuery(id+"F0.imprint","IMPRINT",FACE,{"disambiguationData":[TD([[makeQuery(id+"F0.imprint","IMPRINT",EDGE,{"derivedFrom":sQuery(id+"F0.wireOp",EDGE,"E33.bottom")}),1.0]])]});
            var Q1;
            Q1=makeQuery(id+"F0.imprint","IMPRINT",FACE,{"disambiguationData":[TD([[makeQuery(id+"F0.imprint","IMPRINT",EDGE,{"derivedFrom":sQuery(id+"F0.wireOp",EDGE,"E34.bottom")}),1.0]])]});
            extrude(context, id + "F20", {"entities" : qUnion([Q0, Q1]), "operationType" : NewBodyOperationType.ADD, "depth" : 40 * mm, "offsetDistance" : 25 * mm});
        }
        {
            var Q0;
            Q0=makeQuery(id+"F0.imprint","IMPRINT",FACE,{"disambiguationData":[TD([[makeQuery(id+"F0.imprint","IMPRINT",EDGE,{"derivedFrom":sQuery(id+"F0.wireOp",EDGE,"E35.bottom")}),1.0]])]});
            extrude(context, id + "F21", {"entities" : qUnion([Q0]), "operationType" : NewBodyOperationType.ADD, "depth" : 40 * mm, "offsetDistance" : 25 * mm});
        }
        {
            var Q0;
            Q0=makeQuery(id+"F0.imprint","IMPRINT",FACE,{"disambiguationData":[TD([[makeQuery(id+"F0.imprint","IMPRINT",EDGE,{"derivedFrom":sQuery(id+"F0.wireOp",EDGE,"E36.bottom")}),1.0]])]});
            extrude(context, id + "F22", {"entities" : qUnion([Q0]), "operationType" : NewBodyOperationType.ADD, "depth" : 40 * mm, "offsetDistance" : 25 * mm});
        }
        {
            var Q0;
            Q0=makeQuery(id+"F0.imprint","IMPRINT",FACE,{"disambiguationData":[TD([[makeQuery(id+"F0.imprint","IMPRINT",EDGE,{"derivedFrom":sQuery(id+"F0.wireOp",EDGE,"E37.bottom")}),-1.0]])]});
            var Q1;
            Q1=makeQuery(id+"F0.imprint","IMPRINT",FACE,{"disambiguationData":[TD([[makeQuery(id+"F0.imprint","IMPRINT",EDGE,{"derivedFrom":sQuery(id+"F0.wireOp",EDGE,"E38.bottom")}),1.0]])]});
            extrude(context, id + "F23", {"entities" : qUnion([Q0, Q1]), "operationType" : NewBodyOperationType.ADD, "depth" : 80 * mm, "offsetDistance" : 25 * mm});
        }
        {
            var Q0;
            Q0=makeQuery(id+"F0.imprint","IMPRINT",FACE,{"disambiguationData":[TD([[makeQuery(id+"F0.imprint","IMPRINT",EDGE,{"derivedFrom":sQuery(id+"F0.wireOp",EDGE,"E40.bottom")}),1.0]])]});
            var Q1;
            Q1=makeQuery(id+"F0.imprint","IMPRINT",FACE,{"disambiguationData":[TD([[makeQuery(id+"F0.imprint","IMPRINT",EDGE,{"derivedFrom":sQuery(id+"F0.wireOp",EDGE,"E39.bottom")}),-1.0]])]});
            extrude(context, id + "F24", {"entities" : qUnion([Q0, Q1]), "operationType" : NewBodyOperationType.ADD, "depth" : 40 * mm, "offsetDistance" : 25 * mm});
        }
        {
            var Q0;
            Q0=qCreatedBy(makeId("Top.planeOp"),FACE);
            var sketch = newSketch(context, id + "F25", { "sketchPlane" : qUnion([Q0])});
            skLineSegment(sketch, "E178.bottom", {"start": v(-2966.74, 2913.12) * mm, "end": v(-2056.74, 2913.12) * mm});
            skLineSegment(sketch, "E178.top", {"start": v(-2966.74, 3893.12) * mm, "end": v(-2056.74, 3893.12) * mm});
            skLineSegment(sketch, "E178.left", {"start": v(-2966.74, 2913.12) * mm, "end": v(-2966.74, 3893.12) * mm});
            skLineSegment(sketch, "E178.right", {"start": v(-2056.74, 2913.12) * mm, "end": v(-2056.74, 3893.12) * mm});
            skLineSegment(sketch, "E179", {"start": v(-2886.74, 2913.12) * mm, "end": v(-2886.74, 3040.35) * mm});
            skLineSegment(sketch, "E180", {"start": v(-2966.74, 3893.12) * mm, "end": v(-3777.46, 3893.12) * mm});
            skLineSegment(sketch, "E181.0", {"start": v(-2966.74, 3063.12) * mm, "end": v(-3777.46, 3063.12) * mm});
            skLineSegment(sketch, "E182", {"start": v(-2966.74, 3063.12) * mm, "end": v(-2677.1, 3063.12) * mm});
            skLineSegment(sketch, "E183.0", {"start": v(-2966.74, 3023.12) * mm, "end": v(-2677.1, 3023.12) * mm});
            skLineSegment(sketch, "E184", {"start": v(-2886.74, 3040.35) * mm, "end": v(-2886.74, 3146.98) * mm});
            skLineSegment(sketch, "E185.0", {"start": v(-2966.74, 2983.12) * mm, "end": v(-2677.1, 2983.12) * mm});
            skLineSegment(sketch, "E186.0", {"start": v(-2966.74, 2943.12) * mm, "end": v(-2677.1, 2943.12) * mm});
            skLineSegment(sketch, "E187", {"start": v(-2886.74, 2943.12) * mm, "end": v(-2056.74, 3212.8) * mm});
            skPoint(sketch, "E187.endSnap0", {"position": v(-2821.92, 2943.12) * mm});
            skLineSegment(sketch, "E188", {"start": v(-2886.74, 2983.12) * mm, "end": v(-2056.74, 3586.15) * mm});
            skLineSegment(sketch, "E189", {"start": v(-2886.74, 3023.12) * mm, "end": v(-2254.64, 3893.12) * mm});
            skLineSegment(sketch, "E190", {"start": v(-2886.74, 3063.12) * mm, "end": v(-2617.05, 3893.12) * mm});
            skPoint(sketch, "E190.startSnap0", {"position": v(-2886.74, 3093.67) * mm});
            skLineSegment(sketch, "E191.top", {"start": v(-197.08, 4364.87) * mm, "end": v(152.6, 4364.87) * mm});
            skLineSegment(sketch, "E192", {"start": v(-197.08, 3534.87) * mm, "end": v(-117.08, 3534.87) * mm});
            skLineSegment(sketch, "E193", {"start": v(-117.08, 3534.87) * mm, "end": v(152.6, 4364.87) * mm});
            skLineSegment(sketch, "E194.0", {"start": v(-237.08, 3534.87) * mm, "end": v(-237.08, 4364.87) * mm});
            skLineSegment(sketch, "E195", {"start": v(-197.08, 4364.87) * mm, "end": v(-237.08, 4364.87) * mm});
            skLineSegment(sketch, "E196", {"start": v(-197.08, 3534.87) * mm, "end": v(-237.08, 3534.87) * mm});
            skLineSegment(sketch, "E197.top", {"start": v(1971.74, 4185.4) * mm, "end": v(2334.15, 4185.4) * mm});
            skLineSegment(sketch, "E198", {"start": v(1660, 3355.4) * mm, "end": v(1702.05, 3355.4) * mm});
            skLineSegment(sketch, "E199", {"start": v(1702.05, 3332.65) * mm, "end": v(1702.05, 3355.4) * mm});
            skLineSegment(sketch, "E200", {"start": v(1702.05, 3315.4) * mm, "end": v(2334.15, 4185.4) * mm});
            skLineSegment(sketch, "E201.trimOffspring", {"start": v(1702.05, 3315.4) * mm, "end": v(1702.05, 3332.65) * mm});
            skLineSegment(sketch, "E202.0", {"start": v(1664.01, 3367.77) * mm, "end": v(1929.68, 4185.4) * mm});
            skLineSegment(sketch, "E203", {"start": v(1971.74, 4185.4) * mm, "end": v(1929.68, 4185.4) * mm});
            skLineSegment(sketch, "E204", {"start": v(1664.01, 3367.77) * mm, "end": v(1660, 3355.4) * mm});
            skLineSegment(sketch, "E205", {"start": v(3387.77, 2384.32) * mm, "end": v(3387.77, 2407.08) * mm});
            skLineSegment(sketch, "E206", {"start": v(3387.77, 2327.08) * mm, "end": v(4217.77, 2930.11) * mm});
            skLineSegment(sketch, "E207.trimOffspring", {"start": v(4019.86, 3237.08) * mm, "end": v(4217.77, 3237.08) * mm});
            skLineSegment(sketch, "E208.trimOffspring", {"start": v(4217.77, 2930.11) * mm, "end": v(4217.77, 3237.08) * mm});
            skLineSegment(sketch, "E209.trimOffspring", {"start": v(3387.77, 2327.08) * mm, "end": v(3387.77, 2384.32) * mm});
            skLineSegment(sketch, "E210.0", {"start": v(3367.39, 2407.08) * mm, "end": v(3970.42, 3237.08) * mm});
            skLineSegment(sketch, "E211", {"start": v(4019.86, 3237.08) * mm, "end": v(3970.42, 3237.08) * mm});
            skLineSegment(sketch, "E212", {"start": v(3387.77, 2407.08) * mm, "end": v(3367.39, 2407.08) * mm});
            skLineSegment(sketch, "E213.right", {"start": v(2534.5, 6606.8) * mm, "end": v(2534.5, 6980.15) * mm});
            skLineSegment(sketch, "E214", {"start": v(1704.5, 6337.12) * mm, "end": v(2534.5, 6606.8) * mm});
            skLineSegment(sketch, "E215.0", {"start": v(1704.5, 6426.57) * mm, "end": v(2510.12, 7011.89) * mm});
            skLineSegment(sketch, "E216", {"start": v(1704.5, 6337.12) * mm, "end": v(1704.5, 6426.57) * mm});
            skLineSegment(sketch, "E217", {"start": v(2534.5, 6980.15) * mm, "end": v(2534.5, 7029.6) * mm});
            skLineSegment(sketch, "E218", {"start": v(2510.12, 7011.89) * mm, "end": v(2534.5, 7029.6) * mm});
            skLineSegment(sketch, "E219.bottom", {"start": v(4742.05, 6432.43) * mm, "end": v(5572.05, 6432.43) * mm});
            skLineSegment(sketch, "E219.right", {"start": v(5572.05, 6432.43) * mm, "end": v(5572.05, 6732.11) * mm});
            skLineSegment(sketch, "E220", {"start": v(4742.05, 6432.43) * mm, "end": v(4742.05, 6504.49) * mm});
            skLineSegment(sketch, "E221.0", {"start": v(4742.05, 6504.49) * mm, "end": v(5559.54, 6770.1) * mm});
            skLineSegment(sketch, "E222", {"start": v(5572.05, 6732.11) * mm, "end": v(5572.05, 6774.17) * mm});
            skLineSegment(sketch, "E223", {"start": v(5559.54, 6770.1) * mm, "end": v(5572.05, 6774.17) * mm});
            skLineSegment(sketch, "E224.top", {"start": v(2219.51, 2759.58) * mm, "end": v(2581.92, 2759.58) * mm});
            skLineSegment(sketch, "E225", {"start": v(1907.77, 1929.58) * mm, "end": v(1949.83, 1929.58) * mm});
            skLineSegment(sketch, "E226", {"start": v(1949.83, 1906.82) * mm, "end": v(1949.83, 1929.58) * mm});
            skLineSegment(sketch, "E227", {"start": v(1949.83, 1889.58) * mm, "end": v(2581.92, 2759.58) * mm});
            skLineSegment(sketch, "E228.trimOffspring", {"start": v(1949.83, 1889.58) * mm, "end": v(1949.83, 1906.82) * mm});
            skLineSegment(sketch, "E229.0", {"start": v(1911.79, 1941.94) * mm, "end": v(2177.45, 2759.58) * mm});
            skLineSegment(sketch, "E230", {"start": v(2219.51, 2759.58) * mm, "end": v(2177.45, 2759.58) * mm});
            skLineSegment(sketch, "E231", {"start": v(1911.79, 1941.94) * mm, "end": v(1921.07, 1970.52) * mm});
            skLineSegment(sketch, "E232", {"start": v(1921.07, 1970.52) * mm, "end": v(1907.77, 1929.58) * mm});
            skLineSegment(sketch, "E233.bottom", {"start": v(4578.12, -3806.42) * mm, "end": v(5488.12, -3806.42) * mm});
            skLineSegment(sketch, "E233.top", {"start": v(4578.12, -2826.42) * mm, "end": v(5488.12, -2826.42) * mm});
            skLineSegment(sketch, "E233.left", {"start": v(4578.12, -3806.42) * mm, "end": v(4578.12, -2826.42) * mm});
            skLineSegment(sketch, "E233.right", {"start": v(5488.12, -3806.42) * mm, "end": v(5488.12, -2826.42) * mm});
            skLineSegment(sketch, "E234", {"start": v(4658.12, -3806.42) * mm, "end": v(4658.12, -3679.19) * mm});
            skLineSegment(sketch, "E235", {"start": v(4578.12, -2826.42) * mm, "end": v(3767.4, -2826.42) * mm});
            skLineSegment(sketch, "E236.0", {"start": v(4578.12, -3656.42) * mm, "end": v(3767.4, -3656.42) * mm});
            skLineSegment(sketch, "E237", {"start": v(4578.12, -3656.42) * mm, "end": v(4867.75, -3656.42) * mm});
            skLineSegment(sketch, "E238.0", {"start": v(4578.12, -3696.42) * mm, "end": v(4867.75, -3696.42) * mm});
            skLineSegment(sketch, "E239", {"start": v(4658.12, -3679.19) * mm, "end": v(4658.12, -3572.56) * mm});
            skLineSegment(sketch, "E240.0", {"start": v(4578.12, -3736.42) * mm, "end": v(4867.75, -3736.42) * mm});
            skLineSegment(sketch, "E241.0", {"start": v(4578.12, -3776.42) * mm, "end": v(4867.75, -3776.42) * mm});
            skPoint(sketch, "E242.endSnap0", {"position": v(4722.94, -3776.42) * mm});
            skPoint(sketch, "E243.startSnap0", {"position": v(4658.12, -3625.87) * mm});
            skLineSegment(sketch, "E244", {"start": v(4658.12, -3736.42) * mm, "end": v(6128.46, -3127.39) * mm});
            skLineSegment(sketch, "E245", {"start": v(4658.12, -3696.42) * mm, "end": v(5765.78, -2588.77) * mm});
            skLineSegment(sketch, "E246", {"start": v(4658.12, -3656.42) * mm, "end": v(5047.2, -2717.1) * mm});
            skLineSegment(sketch, "E247.top", {"start": v(7491, -2885.53) * mm, "end": v(7914.8, -2885.53) * mm});
            skLineSegment(sketch, "E248", {"start": v(7491, -3715.53) * mm, "end": v(7571, -3715.53) * mm});
            skLineSegment(sketch, "E249", {"start": v(7571, -3715.53) * mm, "end": v(7914.8, -2885.53) * mm});
            skLineSegment(sketch, "E250.0", {"start": v(7451, -3715.53) * mm, "end": v(7451, -2885.53) * mm});
            skLineSegment(sketch, "E251", {"start": v(7491, -2885.53) * mm, "end": v(7451, -2885.53) * mm});
            skLineSegment(sketch, "E252", {"start": v(7491, -3715.53) * mm, "end": v(7451, -3715.53) * mm});
            skLineSegment(sketch, "E253.top", {"start": v(9526.02, -2587.28) * mm, "end": v(10012.22, -2587.28) * mm});
            skLineSegment(sketch, "E254", {"start": v(9138.92, -3417.28) * mm, "end": v(9182.22, -3417.28) * mm});
            skLineSegment(sketch, "E255", {"start": v(9182.22, -3440.04) * mm, "end": v(9182.22, -3417.28) * mm});
            skLineSegment(sketch, "E256", {"start": v(9182.22, -3457.28) * mm, "end": v(10012.22, -2627.28) * mm});
            skLineSegment(sketch, "E257.trimOffspring", {"start": v(10012.22, -2627.28) * mm, "end": v(10012.22, -2587.28) * mm});
            skLineSegment(sketch, "E258.trimOffspring", {"start": v(9182.22, -3457.28) * mm, "end": v(9182.22, -3440.04) * mm});
            skLineSegment(sketch, "E259.0", {"start": v(9145.28, -3401.94) * mm, "end": v(9482.72, -2587.28) * mm});
            skLineSegment(sketch, "E260", {"start": v(9526.02, -2587.28) * mm, "end": v(9482.72, -2587.28) * mm});
            skLineSegment(sketch, "E261", {"start": v(9145.28, -3401.94) * mm, "end": v(9138.92, -3417.28) * mm});
            skLineSegment(sketch, "E262.right", {"start": v(11711.39, -3267.53) * mm, "end": v(11711.39, -2741.32) * mm});
            skLineSegment(sketch, "E263", {"start": v(10864.82, -3531.32) * mm, "end": v(10881.39, -3531.32) * mm});
            skLineSegment(sketch, "E264", {"start": v(10881.39, -3554.09) * mm, "end": v(10881.39, -3531.32) * mm});
            skLineSegment(sketch, "E265", {"start": v(10881.39, -3611.32) * mm, "end": v(11711.39, -3267.53) * mm});
            skLineSegment(sketch, "E266.trimOffspring", {"start": v(10881.39, -3611.32) * mm, "end": v(10881.39, -3554.09) * mm});
            skLineSegment(sketch, "E267.0", {"start": v(10864.82, -3531.32) * mm, "end": v(11682.96, -2713.18) * mm});
            skLineSegment(sketch, "E268", {"start": v(11711.39, -2741.32) * mm, "end": v(11711.39, -2684.76) * mm});
            skLineSegment(sketch, "E269", {"start": v(11682.96, -2713.18) * mm, "end": v(11711.39, -2684.76) * mm});
            skLineSegment(sketch, "E270.bottom", {"start": v(12969.67, -3695.44) * mm, "end": v(13799.67, -3695.44) * mm});
            skLineSegment(sketch, "E270.right", {"start": v(13799.67, -3695.44) * mm, "end": v(13799.67, -3238.35) * mm});
            skLineSegment(sketch, "E271", {"start": v(12969.67, -3695.44) * mm, "end": v(12969.67, -3582.14) * mm});
            skLineSegment(sketch, "E272.0", {"start": v(12969.67, -3582.14) * mm, "end": v(13783.66, -3244.98) * mm});
            skLineSegment(sketch, "E273", {"start": v(13783.66, -3244.98) * mm, "end": v(13799.67, -3238.35) * mm});
            skSolve(sketch);
        }
        {
            var Q0;
            Q0=makeQuery(id+"F25.imprint","IMPRINT",FACE,{"disambiguationData":[TD([[makeQuery(id+"F25.imprint","IMPRINT",EDGE,{"derivedFrom":sQuery(id+"F25.wireOp",EDGE,"E191.top")}),-1.0]])]});
            extrude(context, id + "F26", {"entities" : qUnion([Q0]), "depth" : 40 * mm, "offsetDistance" : 25 * mm});
        }
        {
            var Q0;
            Q0=makeQuery(id+"F25.imprint","IMPRINT",FACE,{"disambiguationData":[TD([[makeQuery(id+"F25.imprint","IMPRINT",EDGE,{"derivedFrom":sQuery(id+"F25.wireOp",EDGE,"E197.top")}),-1.0]])]});
            extrude(context, id + "F27", {"entities" : qUnion([Q0]), "depth" : 40 * mm, "offsetDistance" : 25 * mm});
        }
        {
            var Q0;
            Q0=makeQuery(id+"F25.imprint","IMPRINT",FACE,{"disambiguationData":[TD([[makeQuery(id+"F25.imprint","IMPRINT",EDGE,{"derivedFrom":sQuery(id+"F25.wireOp",EDGE,"E205")}),-1.0]])]});
            extrude(context, id + "F28", {"entities" : qUnion([Q0]), "depth" : 40 * mm, "offsetDistance" : 25 * mm});
        }
        {
            var Q0;
            Q0=makeQuery(id+"F25.imprint","IMPRINT",FACE,{"disambiguationData":[TD([[makeQuery(id+"F25.imprint","IMPRINT",EDGE,{"derivedFrom":sQuery(id+"F25.wireOp",EDGE,"E213.right")}),1.0]])]});
            extrude(context, id + "F29", {"entities" : qUnion([Q0]), "depth" : 40 * mm, "offsetDistance" : 25 * mm});
        }
        {
            var Q0;
            Q0=makeQuery(id+"F25.imprint","IMPRINT",FACE,{"disambiguationData":[TD([[makeQuery(id+"F25.imprint","IMPRINT",EDGE,{"derivedFrom":sQuery(id+"F25.wireOp",EDGE,"E219.bottom")}),1.0]])]});
            extrude(context, id + "F30", {"entities" : qUnion([Q0]), "depth" : 40 * mm, "offsetDistance" : 25 * mm});
        }
        {
            var Q0;
            Q0=makeQuery(id+"F25.imprint","IMPRINT",FACE,{"disambiguationData":[TD([[makeQuery(id+"F25.imprint","IMPRINT",EDGE,{"derivedFrom":sQuery(id+"F25.wireOp",EDGE,"E224.top")}),-1.0]])]});
            extrude(context, id + "F31", {"entities" : qUnion([Q0]), "depth" : 40 * mm, "offsetDistance" : 25 * mm});
        }
        {
            var Q0;
            Q0=makeQuery(id+"F4.imprint","IMPRINT",FACE,{"disambiguationData":[TD([[makeQuery(id+"F4.imprint","IMPRINT",EDGE,{"derivedFrom":sQuery(id+"F4.wireOp",EDGE,"E157.top")}),-1.0]])]});
            extrude(context, id + "F32", {"entities" : qUnion([Q0]), "depth" : 40 * mm, "offsetDistance" : 25 * mm});
        }
        {
            var Q0;
            Q0=makeQuery(id+"F4.imprint","IMPRINT",FACE,{"disambiguationData":[TD([[makeQuery(id+"F4.imprint","IMPRINT",EDGE,{"derivedFrom":sQuery(id+"F4.wireOp",EDGE,"E164.top")}),-1.0]])]});
            extrude(context, id + "F33", {"entities" : qUnion([Q0]), "depth" : 40 * mm, "offsetDistance" : 25 * mm});
        }
        {
            var Q0;
            Q0=makeQuery(id+"F4.imprint","IMPRINT",FACE,{"disambiguationData":[TD([[makeQuery(id+"F4.imprint","IMPRINT",EDGE,{"derivedFrom":sQuery(id+"F4.wireOp",EDGE,"E168.left")}),-1.0]])]});
            extrude(context, id + "F34", {"entities" : qUnion([Q0]), "depth" : 40 * mm, "offsetDistance" : 25 * mm});
        }
        {
            var Q0;
            Q0=makeQuery(id+"F4.imprint","IMPRINT",FACE,{"disambiguationData":[TD([[makeQuery(id+"F4.imprint","IMPRINT",EDGE,{"derivedFrom":sQuery(id+"F4.wireOp",EDGE,"E175.bottom")}),1.0]])]});
            extrude(context, id + "F35", {"entities" : qUnion([Q0]), "depth" : 40 * mm, "offsetDistance" : 25 * mm});
        }
        {
            var Q0;
            Q0=makeQuery(id+"F0.imprint","IMPRINT",FACE,{"disambiguationData":[TD([[makeQuery(id+"F0.imprint","IMPRINT",EDGE,{"derivedFrom":sQuery(id+"F0.wireOp",EDGE,"E41.bottom")}),1.0]])]});
            var Q1;
            Q1=makeQuery(id+"F0.imprint","IMPRINT",FACE,{"disambiguationData":[TD([[makeQuery(id+"F0.imprint","IMPRINT",EDGE,{"derivedFrom":sQuery(id+"F0.wireOp",EDGE,"E42.bottom")}),1.0]])]});
            extrude(context, id + "F36", {"entities" : qUnion([Q0, Q1]), "operationType" : NewBodyOperationType.ADD, "depth" : 40 * mm, "offsetDistance" : 25 * mm});
        }
        {
            var Q0;
            Q0=makeQuery(id+"F0.imprint","IMPRINT",FACE,{"disambiguationData":[TD([[makeQuery(id+"F0.imprint","IMPRINT",EDGE,{"derivedFrom":sQuery(id+"F0.wireOp",EDGE,"E43.bottom")}),1.0]])]});
            var Q1;
            Q1=makeQuery(id+"F0.imprint","IMPRINT",FACE,{"disambiguationData":[TD([[makeQuery(id+"F0.imprint","IMPRINT",EDGE,{"derivedFrom":sQuery(id+"F0.wireOp",EDGE,"E44.bottom")}),1.0]])]});
            extrude(context, id + "F37", {"entities" : qUnion([Q0, Q1]), "operationType" : NewBodyOperationType.ADD, "depth" : 40 * mm, "offsetDistance" : 25 * mm});
        }
        {
            var Q0;
            Q0=makeQuery(id+"F0.imprint","IMPRINT",FACE,{"disambiguationData":[TD([[makeQuery(id+"F0.imprint","IMPRINT",EDGE,{"derivedFrom":sQuery(id+"F0.wireOp",EDGE,"E45.bottom")}),1.0]])]});
            var Q1;
            Q1=makeQuery(id+"F0.imprint","IMPRINT",FACE,{"disambiguationData":[TD([[makeQuery(id+"F0.imprint","IMPRINT",EDGE,{"derivedFrom":sQuery(id+"F0.wireOp",EDGE,"E46.bottom")}),1.0]])]});
            extrude(context, id + "F38", {"entities" : qUnion([Q0, Q1]), "operationType" : NewBodyOperationType.ADD, "depth" : 40 * mm, "offsetDistance" : 25 * mm});
        }
        {
            var Q0;
            Q0=makeQuery(id+"F0.imprint","IMPRINT",FACE,{"disambiguationData":[TD([[makeQuery(id+"F0.imprint","IMPRINT",EDGE,{"derivedFrom":sQuery(id+"F0.wireOp",EDGE,"E47.bottom")}),1.0]])]});
            var Q1;
            Q1=makeQuery(id+"F0.imprint","IMPRINT",FACE,{"disambiguationData":[TD([[makeQuery(id+"F0.imprint","IMPRINT",EDGE,{"derivedFrom":sQuery(id+"F0.wireOp",EDGE,"E48.bottom")}),1.0]])]});
            extrude(context, id + "F39", {"entities" : qUnion([Q0, Q1]), "operationType" : NewBodyOperationType.ADD, "depth" : 40 * mm, "offsetDistance" : 25 * mm});
        }
        {
            var Q0;
            Q0=makeQuery(id+"F0.imprint","IMPRINT",FACE,{"disambiguationData":[TD([[makeQuery(id+"F0.imprint","IMPRINT",EDGE,{"derivedFrom":sQuery(id+"F0.wireOp",EDGE,"E49.bottom")}),1.0]])]});
            extrude(context, id + "F40", {"entities" : qUnion([Q0]), "operationType" : NewBodyOperationType.ADD, "depth" : 40 * mm, "offsetDistance" : 25 * mm});
        }
        {
            var Q0;
            Q0=makeQuery(id+"F25.imprint","IMPRINT",FACE,{"disambiguationData":[TD([[makeQuery(id+"F25.imprint","IMPRINT",EDGE,{"derivedFrom":sQuery(id+"F25.wireOp",EDGE,"E247.top")}),-1.0]])]});
            extrude(context, id + "F41", {"entities" : qUnion([Q0]), "depth" : 40 * mm, "offsetDistance" : 25 * mm});
        }
        {
            var Q0;
            Q0=makeQuery(id+"F25.imprint","IMPRINT",FACE,{"disambiguationData":[TD([[makeQuery(id+"F25.imprint","IMPRINT",EDGE,{"derivedFrom":sQuery(id+"F25.wireOp",EDGE,"E253.top")}),-1.0]])]});
            extrude(context, id + "F42", {"entities" : qUnion([Q0]), "depth" : 40 * mm, "offsetDistance" : 25 * mm});
        }
        {
            var Q0;
            Q0=makeQuery(id+"F25.imprint","IMPRINT",FACE,{"disambiguationData":[TD([[makeQuery(id+"F25.imprint","IMPRINT",EDGE,{"derivedFrom":sQuery(id+"F25.wireOp",EDGE,"E262.right")}),1.0]])]});
            extrude(context, id + "F43", {"entities" : qUnion([Q0]), "depth" : 40 * mm, "offsetDistance" : 25 * mm});
        }
        {
            var Q0;
            Q0=makeQuery(id+"F25.imprint","IMPRINT",FACE,{"disambiguationData":[TD([[makeQuery(id+"F25.imprint","IMPRINT",EDGE,{"derivedFrom":sQuery(id+"F25.wireOp",EDGE,"E270.bottom")}),1.0]])]});
            extrude(context, id + "F44", {"entities" : qUnion([Q0]), "depth" : 40 * mm, "offsetDistance" : 25 * mm});
        }
        {
            var Q0;
            Q0=qCreatedBy(makeId("Top.planeOp"),FACE);
            var sketch = newSketch(context, id + "F45", { "sketchPlane" : qUnion([Q0])});
            skLineSegment(sketch, "E274.bottom", {"start": v(-2231.5, 228.06) * mm, "end": v(1688.5, 228.06) * mm});
            skLineSegment(sketch, "E274.top", {"start": v(-2231.5, -21.94) * mm, "end": v(1688.5, -21.94) * mm});
            skLineSegment(sketch, "E274.left", {"start": v(-2231.5, 228.06) * mm, "end": v(-2231.5, -21.94) * mm});
            skLineSegment(sketch, "E274.right", {"start": v(1688.5, 228.06) * mm, "end": v(1688.5, -21.94) * mm});
            skLineSegment(sketch, "E275.bottom", {"start": v(-2231.5, 228.06) * mm, "end": v(-2481.5, 228.06) * mm});
            skLineSegment(sketch, "E275.top", {"start": v(-2231.5, -1361.94) * mm, "end": v(-2481.5, -1361.94) * mm});
            skLineSegment(sketch, "E275.left", {"start": v(-2231.5, 228.06) * mm, "end": v(-2231.5, -1361.94) * mm});
            skLineSegment(sketch, "E275.right", {"start": v(-2481.5, 228.06) * mm, "end": v(-2481.5, -1361.94) * mm});
            skLineSegment(sketch, "E276.bottom", {"start": v(1688.5, 228.06) * mm, "end": v(1938.5, 228.06) * mm});
            skLineSegment(sketch, "E276.top", {"start": v(1688.5, -1361.94) * mm, "end": v(1938.5, -1361.94) * mm});
            skLineSegment(sketch, "E276.left", {"start": v(1688.5, 228.06) * mm, "end": v(1688.5, -1361.94) * mm});
            skLineSegment(sketch, "E276.right", {"start": v(1938.5, 228.06) * mm, "end": v(1938.5, -1361.94) * mm});
            skLineSegment(sketch, "E277.bottom", {"start": v(-2764.78, 1761.75) * mm, "end": v(1655.22, 1761.75) * mm});
            skLineSegment(sketch, "E277.top", {"start": v(-2764.78, 1331.75) * mm, "end": v(1655.22, 1331.75) * mm});
            skLineSegment(sketch, "E277.left", {"start": v(-2764.78, 1761.75) * mm, "end": v(-2764.78, 1331.75) * mm});
            skLineSegment(sketch, "E277.right", {"start": v(1655.22, 1761.75) * mm, "end": v(1655.22, 1331.75) * mm});
            skLineSegment(sketch, "E278.bottom", {"start": v(-2773.87, 4000.27) * mm, "end": v(-2523.87, 4000.27) * mm});
            skLineSegment(sketch, "E278.top", {"start": v(-2773.87, 2840.27) * mm, "end": v(-2523.87, 2840.27) * mm});
            skLineSegment(sketch, "E278.left", {"start": v(-2773.87, 4000.27) * mm, "end": v(-2773.87, 2840.27) * mm});
            skLineSegment(sketch, "E278.right", {"start": v(-2523.87, 4000.27) * mm, "end": v(-2523.87, 2840.27) * mm});
            skLineSegment(sketch, "E279.bottom", {"start": v(-15195.3, 3645.53) * mm, "end": v(-10775.3, 3645.53) * mm});
            skLineSegment(sketch, "E279.top", {"start": v(-15195.3, 3225.53) * mm, "end": v(-10775.3, 3225.53) * mm});
            skLineSegment(sketch, "E279.left", {"start": v(-15195.3, 3645.53) * mm, "end": v(-15195.3, 3225.53) * mm});
            skLineSegment(sketch, "E279.right", {"start": v(-10775.3, 3645.53) * mm, "end": v(-10775.3, 3225.53) * mm});
            skSolve(sketch);
        }
        {
            var Q0;
            Q0=makeQuery(id+"F45.imprint","IMPRINT",FACE,{"disambiguationData":[TD([[makeQuery(id+"F45.imprint","IMPRINT",EDGE,{"derivedFrom":sQuery(id+"F45.wireOp",EDGE,"E274.bottom")}),-1.0]])]});
            extrude(context, id + "F46", {"entities" : qUnion([Q0]), "depth" : 2640 * mm, "offsetDistance" : 25 * mm});
        }
        {
            var Q0;
            {var subQ3=sQuery(id+"F45.wireOp",EDGE,"E275.bottom");Q0=makeQuery(id+"F45.imprint","IMPRINT",FACE,{"disambiguationData":[TD([[makeQuery(id+"F45.imprint","IMPRINT",EDGE,{"derivedFrom":subQ3}),1.0]])]});}
            extrude(context, id + "F47", {"entities" : qUnion([Q0]), "depth" : 2640 * mm, "offsetDistance" : 25 * mm});
        }
        {
            var Q0;
            {var subQ3=sQuery(id+"F45.wireOp",EDGE,"E276.bottom");Q0=makeQuery(id+"F45.imprint","IMPRINT",FACE,{"disambiguationData":[TD([[makeQuery(id+"F45.imprint","IMPRINT",EDGE,{"derivedFrom":subQ3}),-1.0]])]});}
            extrude(context, id + "F48", {"entities" : qUnion([Q0]), "operationType" : NewBodyOperationType.ADD, "depth" : 2640 * mm, "offsetDistance" : 25 * mm});
        }
        {
            var Q0;
            Q0=makeQuery(id+"F45.imprint","IMPRINT",FACE,{"disambiguationData":[TD([[makeQuery(id+"F45.imprint","IMPRINT",EDGE,{"derivedFrom":sQuery(id+"F45.wireOp",EDGE,"E277.bottom")}),-1.0]])]});
            extrude(context, id + "F49", {"entities" : qUnion([Q0]), "depth" : 220 * mm, "offsetDistance" : 25 * mm});
        }
        {
            var Q0;
            Q0=makeQuery(id+"F45.imprint","IMPRINT",FACE,{"disambiguationData":[TD([[makeQuery(id+"F45.imprint","IMPRINT",EDGE,{"derivedFrom":sQuery(id+"F45.wireOp",EDGE,"E278.bottom")}),-1.0]])]});
            extrude(context, id + "F50", {"entities" : qUnion([Q0]), "depth" : 220 * mm, "offsetDistance" : 25 * mm});
        }
        {
            var Q0;
            Q0=makeQuery(id+"F45.imprint","IMPRINT",FACE,{"disambiguationData":[TD([[makeQuery(id+"F45.imprint","IMPRINT",EDGE,{"derivedFrom":sQuery(id+"F45.wireOp",EDGE,"E279.bottom")}),-1.0]])]});
            extrude(context, id + "F51", {"entities" : qUnion([Q0]), "depth" : 500 * mm, "offsetDistance" : 25 * mm});
        }
        {
            var Q0;
            Q0=qCreatedBy(makeId("Right.planeOp"),FACE);
            var sketch = newSketch(context, id + "F52", { "sketchPlane" : qUnion([Q0])});
            skCircle(sketch, "E280", {"center": v(-3447.27, 4156.33) * mm, "radius": 25 * mm});
            skSolve(sketch);
        }
        {
            var Q0;
            Q0=makeQuery(id+"F52.imprint","IMPRINT",FACE,{"disambiguationData":[TD([[makeQuery(id+"F52.imprint","IMPRINT",EDGE,{"derivedFrom":sQuery(id+"F52.wireOp",EDGE,"E280")}),1.0]])]});
            extrude(context, id + "F53", {"entities" : qUnion([Q0]), "depth" : 3920 * mm, "offsetDistance" : 25 * mm});
        }
    });